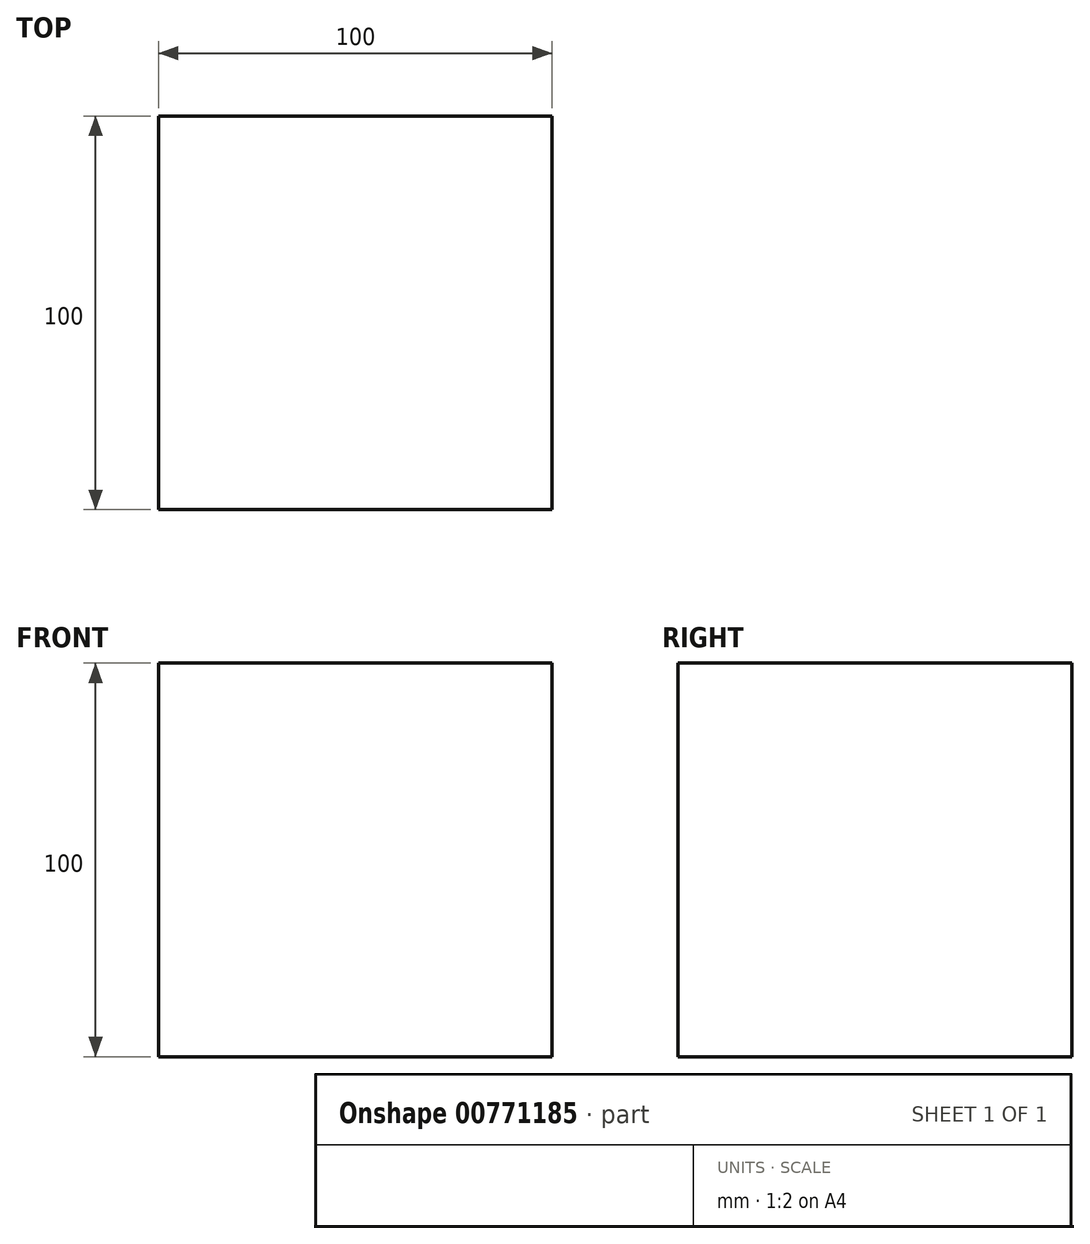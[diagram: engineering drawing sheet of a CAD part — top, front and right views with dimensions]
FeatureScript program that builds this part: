
annotation { "Feature Type Name" : "Feature", "Feature Type Description" : "" }
export const myFeature = defineFeature(function(context is Context, id is Id, definition is map)
    precondition{}
    {
        {
            var Q0;
            Q0=qCreatedBy(makeId("Front.planeOp"),FACE);
            var sketch = newSketch(context, id + "F0", { "sketchPlane" : qUnion([Q0])});
            skLineSegment(sketch, "E0.bottom", {"start": v(50, 50) * mm, "end": v(-50, 50) * mm});
            skLineSegment(sketch, "E0.top", {"start": v(50, -50) * mm, "end": v(-50, -50) * mm});
            skLineSegment(sketch, "E0.left", {"start": v(50, 50) * mm, "end": v(50, -50) * mm});
            skLineSegment(sketch, "E0.right", {"start": v(-50, 50) * mm, "end": v(-50, -50) * mm});
            skPoint(sketch, "E0.middle", {"position": v(0, 0) * mm});
            skSolve(sketch);
        }
        {
            var Q0;
            Q0=makeQuery(id+"F0.imprint","IMPRINT",FACE,{"disambiguationData":[TD([[makeQuery(id+"F0.imprint","IMPRINT",EDGE,{"derivedFrom":sQuery(id+"F0.wireOp",EDGE,"E0.bottom")}),1.0]])]});
            extrude(context, id + "F1", {"entities" : qUnion([Q0]), "depth" : 100 * mm, "offsetDistance" : 25 * mm});
        }
    });
